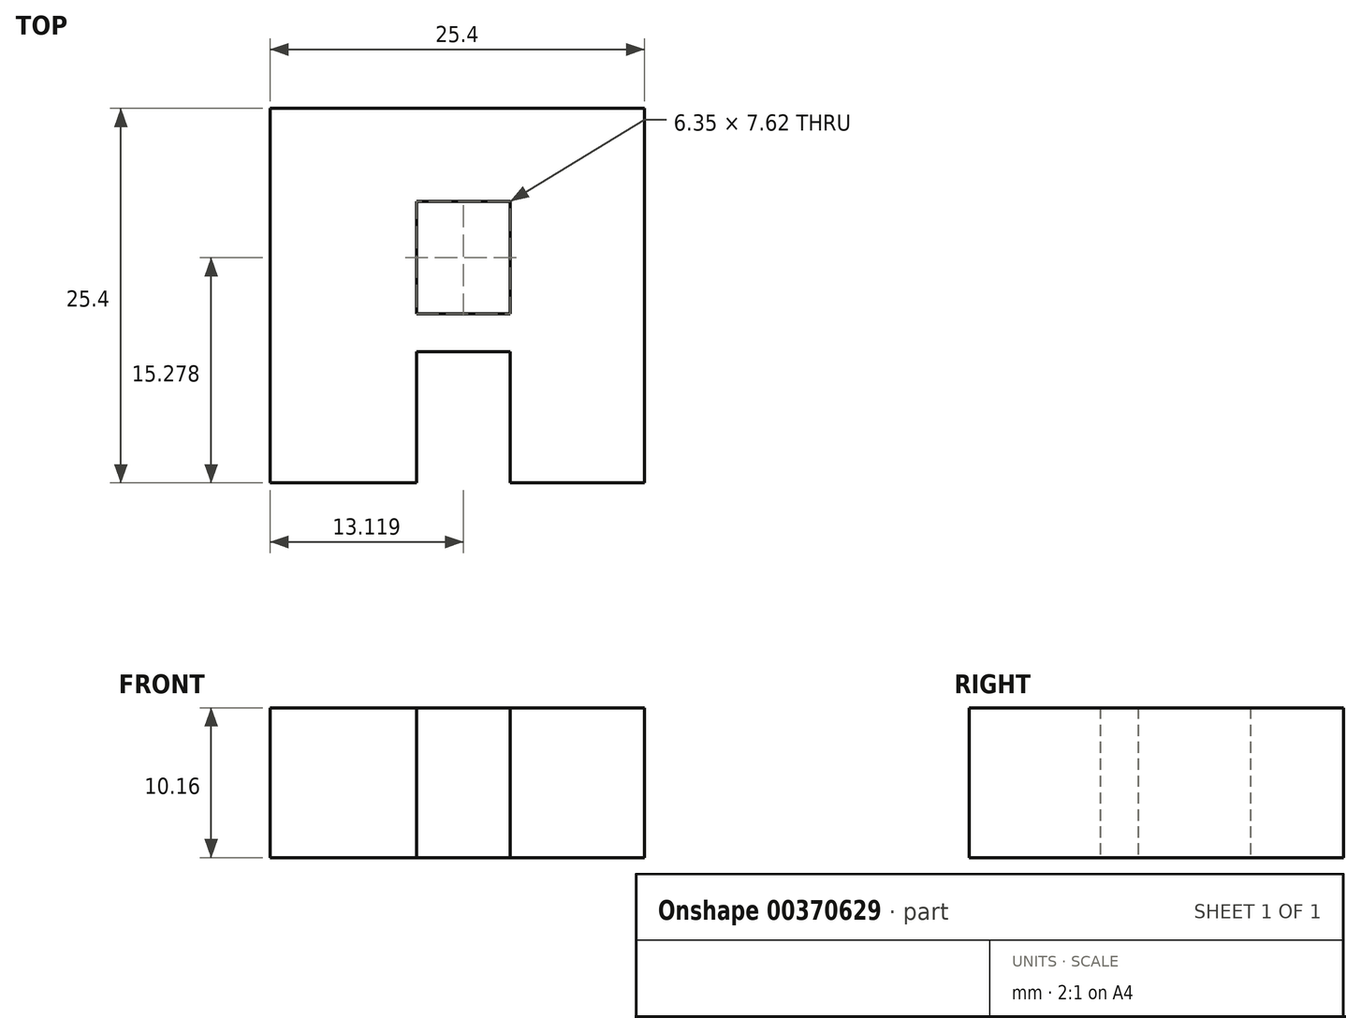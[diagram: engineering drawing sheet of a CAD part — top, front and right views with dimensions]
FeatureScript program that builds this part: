
annotation { "Feature Type Name" : "Feature", "Feature Type Description" : "" }
export const myFeature = defineFeature(function(context is Context, id is Id, definition is map)
    precondition{}
    {
        {
            var Q0;
            Q0=qCreatedBy(makeId("Top.planeOp"),FACE);
            var sketch = newSketch(context, id + "F0", { "sketchPlane" : qUnion([Q0])});
            skLineSegment(sketch, "E0", {"start": v(0, 0) * mm, "end": v(0, 25.4) * mm});
            skLineSegment(sketch, "E1", {"start": v(0, 25.4) * mm, "end": v(25.4, 25.4) * mm});
            skLineSegment(sketch, "E2", {"start": v(25.4, 25.4) * mm, "end": v(25.4, 0) * mm});
            skLineSegment(sketch, "E3", {"start": v(25.4, 0) * mm, "end": v(16.3, 0) * mm});
            skLineSegment(sketch, "E4", {"start": v(16.3, 0) * mm, "end": v(16.3, 8.9) * mm});
            skLineSegment(sketch, "E5", {"start": v(16.3, 8.9) * mm, "end": v(9.94, 8.9) * mm});
            skLineSegment(sketch, "E6", {"start": v(9.94, 8.9) * mm, "end": v(9.94, 0) * mm});
            skLineSegment(sketch, "E7", {"start": v(9.94, 11.47) * mm, "end": v(9.94, 19.09) * mm});
            skLineSegment(sketch, "E8", {"start": v(9.94, 19.09) * mm, "end": v(16.3, 19.09) * mm});
            skLineSegment(sketch, "E9", {"start": v(16.3, 19.09) * mm, "end": v(16.3, 11.47) * mm});
            skLineSegment(sketch, "E10", {"start": v(9.94, 0) * mm, "end": v(0, 0) * mm});
            skLineSegment(sketch, "E11", {"start": v(9.94, 11.47) * mm, "end": v(16.3, 11.47) * mm});
            skSolve(sketch);
        }
        {
            var Q0;
            Q0 = qSketchRegion(id + "F0", true);
            extrude(context, id + "F1", {"entities" : qUnion([Q0]), "depth" : 10.16 * mm});
        }
    });
